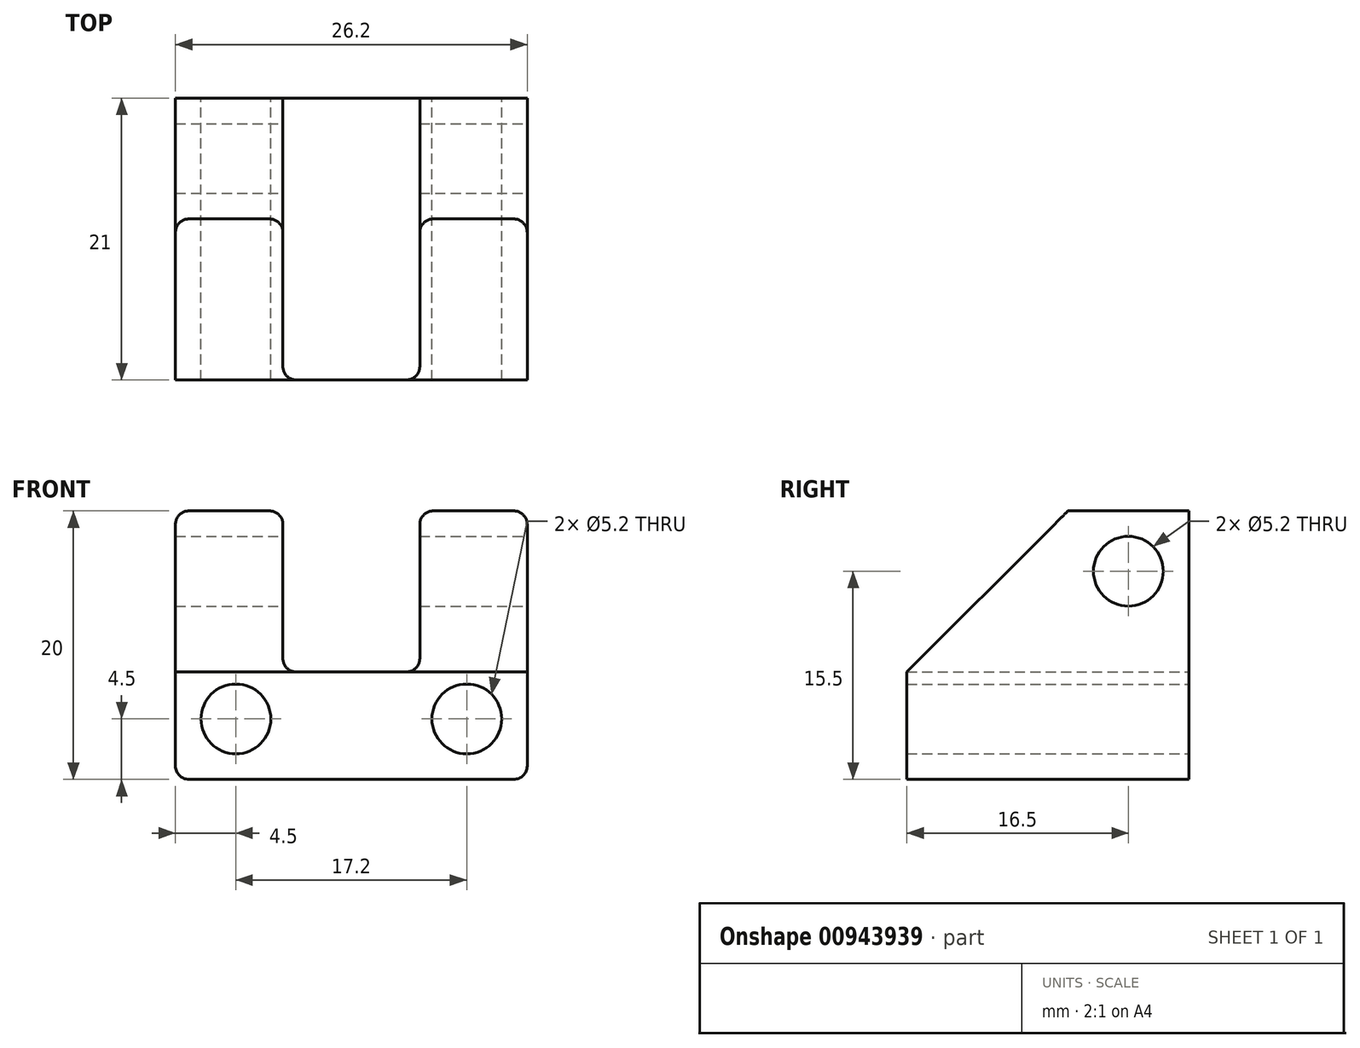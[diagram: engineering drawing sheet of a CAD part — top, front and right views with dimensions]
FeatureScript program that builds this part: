
annotation { "Feature Type Name" : "Feature", "Feature Type Description" : "" }
export const myFeature = defineFeature(function(context is Context, id is Id, definition is map)
    precondition{}
    {
        {
            var Q0;
            Q0=qCreatedBy(makeId("Front.planeOp"),FACE);
            var sketch = newSketch(context, id + "F0", { "sketchPlane" : qUnion([Q0])});
            skLineSegment(sketch, "E0.bottom", {"start": v(-3.5, 15.5) * mm, "end": v(4.5, 15.5) * mm});
            skLineSegment(sketch, "E0.left", {"start": v(-3.5, 15.5) * mm, "end": v(-3.5, 3.5) * mm});
            skLineSegment(sketch, "E0.right", {"start": v(4.5, 15.5) * mm, "end": v(4.5, -4.5) * mm});
            skLineSegment(sketch, "E1.MirrorCS", {"start": v(-13.7, 15.5) * mm, "end": v(-21.7, 15.5) * mm});
            skLineSegment(sketch, "E2.MirrorCS", {"start": v(-13.7, 15.5) * mm, "end": v(-13.7, 3.5) * mm});
            skLineSegment(sketch, "E3.MirrorCS", {"start": v(-21.7, 15.5) * mm, "end": v(-21.7, -4.5) * mm});
            skLineSegment(sketch, "E4", {"start": v(-13.7, 3.5) * mm, "end": v(-3.5, 3.5) * mm});
            skLineSegment(sketch, "E5", {"start": v(-21.7, -4.5) * mm, "end": v(4.5, -4.5) * mm});
            skSolve(sketch);
        }
        {
            var Q0;
            Q0 = qSketchRegion(id + "F0", true);
            var Q1;
            Q1 = qConstructionFilter(qBodyType(qCreatedBy(id + "F0" ,EDGE), BodyType.WIRE), ConstructionObject.NO);
            extrude(context, id + "F1", {"entities" : qUnion([Q0]), "surfaceEntities" : qUnion([Q1]), "depth" : 8.5 * mm, "offsetDistance" : 25 * mm, "hasSecondDirection" : true, "secondDirectionOppositeDirection" : true, "secondDirectionDepth" : 12.5 * mm});
        }
        {
            var Q0;
            Q0=qCreatedBy(makeId("Front.planeOp"),FACE);
            var sketch = newSketch(context, id + "F2", { "sketchPlane" : qUnion([Q0])});
            skCircle(sketch, "E6", {"center": v(0, 0) * mm, "radius": 2.6 * mm});
            skCircle(sketch, "E7", {"center": v(-17.2, 0) * mm, "radius": 2.6 * mm});
            skSolve(sketch);
        }
        {
            var Q0;
            Q0 = qSketchRegion(id + "F2", true);
            extrude(context, id + "F3", {"entities" : qUnion([Q0]), "operationType" : NewBodyOperationType.REMOVE, "depth" : 13 * mm, "offsetDistance" : 25 * mm, "hasSecondDirection" : true, "secondDirectionOppositeDirection" : true, "secondDirectionDepth" : 13 * mm});
        }
        {
            var Q0;
            Q0=qCreatedBy(makeId("Right.planeOp"),FACE);
            var sketch = newSketch(context, id + "F4", { "sketchPlane" : qUnion([Q0])});
            skCircle(sketch, "E8", {"center": v(8, 11) * mm, "radius": 2.6 * mm});
            skSolve(sketch);
        }
        {
            var Q0;
            Q0 = qSketchRegion(id + "F4", true);
            extrude(context, id + "F5", {"entities" : qUnion([Q0]), "operationType" : NewBodyOperationType.REMOVE, "oppositeDirection" : true, "depth" : 25 * mm, "offsetDistance" : 25 * mm, "hasSecondDirection" : true, "secondDirectionOppositeDirection" : false, "secondDirectionDepth" : 25 * mm});
        }
        {
            var Q0;
            Q0=makeQuery(id+"F1.opExtrude","CAP_EDGE",EDGE,{"disambiguationData":[OSD([sQuery(id+"F0.wireOp",EDGE,"E1.MirrorCS")])],"isStart":false});
            var Q1;
            Q1=makeQuery(id+"F1.opExtrude","CAP_EDGE",EDGE,{"disambiguationData":[OSD([sQuery(id+"F0.wireOp",EDGE,"E0.bottom")])],"isStart":false});
            chamfer(context, id + "F6", {"entities" : qUnion([Q0, Q1]), "width" : 12 * mm, "tangentPropagation" : true});
        }
        {
            var Q0;
            Q0=makeQuery(id+"F1.opExtrude","SWEPT_EDGE",EDGE,{"disambiguationData":[OSD([sQuery(id+"F0.wireOp",EDGE,"E0.right"),sQuery(id+"F0.wireOp",EDGE,"E5")])]});
            var Q1;
            Q1=makeQuery(id+"F1.opExtrude","SWEPT_EDGE",EDGE,{"disambiguationData":[OSD([sQuery(id+"F0.wireOp",EDGE,"E0.bottom"),sQuery(id+"F0.wireOp",EDGE,"E0.right")])]});
            var Q2;
            Q2=makeQuery(id+"F1.opExtrude","SWEPT_EDGE",EDGE,{"disambiguationData":[OSD([sQuery(id+"F0.wireOp",EDGE,"E3.MirrorCS"),sQuery(id+"F0.wireOp",EDGE,"E5")])]});
            var Q3;
            Q3=makeQuery(id+"F1.opExtrude","SWEPT_EDGE",EDGE,{"disambiguationData":[OSD([sQuery(id+"F0.wireOp",EDGE,"E1.MirrorCS"),sQuery(id+"F0.wireOp",EDGE,"E3.MirrorCS")])]});
            var Q4;
            Q4=makeQuery(id+"F1.opExtrude","SWEPT_EDGE",EDGE,{"disambiguationData":[OSD([sQuery(id+"F0.wireOp",EDGE,"E1.MirrorCS"),sQuery(id+"F0.wireOp",EDGE,"E2.MirrorCS")])]});
            var Q5;
            Q5=makeQuery(id+"F1.opExtrude","SWEPT_EDGE",EDGE,{"disambiguationData":[OSD([sQuery(id+"F0.wireOp",EDGE,"E0.left"),sQuery(id+"F0.wireOp",EDGE,"E4")])]});
            var Q6;
            Q6=makeQuery(id+"F1.opExtrude","SWEPT_EDGE",EDGE,{"disambiguationData":[OSD([sQuery(id+"F0.wireOp",EDGE,"E2.MirrorCS"),sQuery(id+"F0.wireOp",EDGE,"E4")])]});
            var Q7;
            Q7=makeQuery(id+"F1.opExtrude","SWEPT_EDGE",EDGE,{"disambiguationData":[OSD([sQuery(id+"F0.wireOp",EDGE,"E0.bottom"),sQuery(id+"F0.wireOp",EDGE,"E0.left")])]});
            fillet(context, id + "F7", {"entities" : qUnion([Q0, Q1, Q2, Q3, Q4, Q5, Q6, Q7]), "radius" : 1 * mm, "tangentPropagation" : true, "allowEdgeOverflow" : false});
        }
    });
